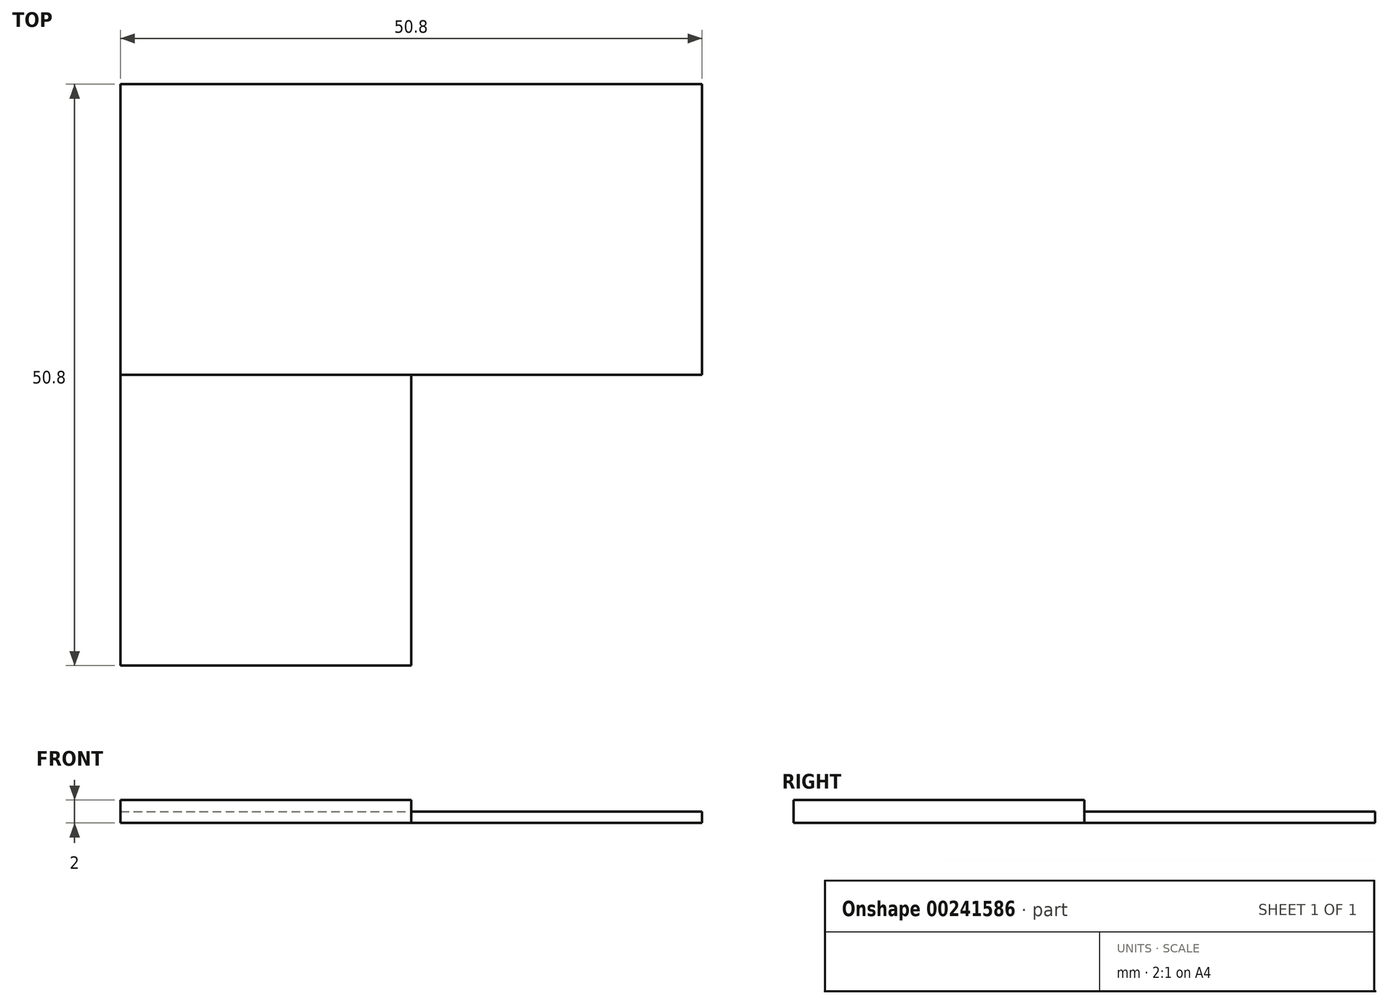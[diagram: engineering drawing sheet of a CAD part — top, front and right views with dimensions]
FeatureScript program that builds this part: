
annotation { "Feature Type Name" : "Feature", "Feature Type Description" : "" }
export const myFeature = defineFeature(function(context is Context, id is Id, definition is map)
    precondition{}
    {
        {
            assignVariable(context, id + "F0", {"name" : "x", "anyValue" : 1});
        }
        {
            var Q0;
            Q0=qCreatedBy(makeId("Top.planeOp"),FACE);
            var sketch = newSketch(context, id + "F1", { "sketchPlane" : qUnion([Q0])});
            skLineSegment(sketch, "E0.bottom", {"start": v(25.4, 25.4) * mm, "end": v(-25.4, 25.4) * mm});
            skLineSegment(sketch, "E0.top", {"start": v(25.4, -25.4) * mm, "end": v(-25.4, -25.4) * mm});
            skLineSegment(sketch, "E0.left", {"start": v(25.4, 25.4) * mm, "end": v(25.4, -25.4) * mm});
            skLineSegment(sketch, "E0.right", {"start": v(-25.4, 25.4) * mm, "end": v(-25.4, -25.4) * mm});
            skPoint(sketch, "E0.middle", {"position": v(0, 0) * mm});
            skSolve(sketch);
        }
        {
            var Q0;
            Q0=makeQuery(id+"F1.imprint","IMPRINT",FACE,{"disambiguationData":[TD([[makeQuery(id+"F1.imprint","IMPRINT",EDGE,{"derivedFrom":sQuery(id+"F1.wireOp",EDGE,"E0.bottom")}),1.0]])]});
            extrude(context, id + "F2", {"entities" : qUnion([Q0]), "depth" : (getVariable(context, 'x')) * mm});
        }
        {
            var Q0;
            Q0=makeQuery(id+"F2.opExtrude","CAP_FACE",FACE,{"disambiguationData":[OSD([sQuery(id+"F1.wireOp",EDGE,"E0.bottom"),sQuery(id+"F1.wireOp",EDGE,"E0.top"),sQuery(id+"F1.wireOp",EDGE,"E0.left"),sQuery(id+"F1.wireOp",EDGE,"E0.right")])],"isStart":false});
            var sketch = newSketch(context, id + "F3", { "sketchPlane" : qUnion([Q0])});
            skLineSegment(sketch, "E1.bottom", {"start": v(25.4, -25.4) * mm, "end": v(0, -25.4) * mm});
            skLineSegment(sketch, "E1.top", {"start": v(25.4, 0) * mm, "end": v(0, 0) * mm});
            skLineSegment(sketch, "E1.left", {"start": v(25.4, -25.4) * mm, "end": v(25.4, 0) * mm});
            skLineSegment(sketch, "E1.right", {"start": v(0, -25.4) * mm, "end": v(0, 0) * mm});
            skSolve(sketch);
        }
        {
            var Q0;
            Q0 = qSketchRegion(id + "F3", true);
            extrude(context, id + "F4", {"entities" : qUnion([Q0]), "operationType" : NewBodyOperationType.REMOVE, "oppositeDirection" : true, "depth" : (getVariable(context, 'x')) * mm});
        }
        {
            var Q0;
            Q0=makeQuery(id+"F2.opExtrude","CAP_FACE",FACE,{"disambiguationData":[OSD([sQuery(id+"F1.wireOp",EDGE,"E0.bottom"),sQuery(id+"F1.wireOp",EDGE,"E0.top"),sQuery(id+"F1.wireOp",EDGE,"E0.left"),sQuery(id+"F1.wireOp",EDGE,"E0.right")])],"isStart":false});
            var sketch = newSketch(context, id + "F5", { "sketchPlane" : qUnion([Q0])});
            skLineSegment(sketch, "E2.bottom", {"start": v(-25.4, -25.4) * mm, "end": v(0, -25.4) * mm});
            skLineSegment(sketch, "E2.top", {"start": v(-25.4, 0) * mm, "end": v(0, 0) * mm});
            skLineSegment(sketch, "E2.left", {"start": v(-25.4, -25.4) * mm, "end": v(-25.4, 0) * mm});
            skLineSegment(sketch, "E2.right", {"start": v(0, -25.4) * mm, "end": v(0, 0) * mm});
            skSolve(sketch);
        }
        {
            var Q0;
            Q0=makeQuery(id+"F5.imprint","IMPRINT",FACE,{"disambiguationData":[TD([[makeQuery(id+"F5.imprint","IMPRINT",EDGE,{"derivedFrom":sQuery(id+"F5.wireOp",EDGE,"E2.bottom")}),-1.0]])]});
            extrude(context, id + "F6", {"entities" : qUnion([Q0]), "operationType" : NewBodyOperationType.ADD, "depth" : (getVariable(context, 'x')) * mm});
        }
    });
